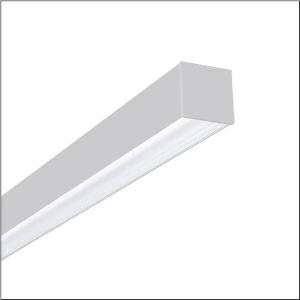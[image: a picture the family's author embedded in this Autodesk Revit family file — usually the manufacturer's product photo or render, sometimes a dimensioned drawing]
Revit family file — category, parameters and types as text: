
# Revit family: silica_r_5mx31bd1w4a_74d2
name_source: partatom
category: Lighting Fixtures
units: mm (PartAtom-declared; Revit-internal decimal feet)

## family parameters
Cut with Voids When Loaded = No
Host = Face
Light Source = No
Part Type = Normal
Room Calculation Point = No
Round Connector Dimension = Use Diameter
Shared = No

## types (1)
- --- (1 x LED, 7070 lm, 45.6 W, 4000K)
    Apparent Load = 46 VA
    CIE Flux Codes = 82 97 100 70 100
    Color Rendering = 80
    Color Temperature = 4000K
    Default Elevation = 1800 mm
    Description = Silica®, office luminaire, of aluminium, light emission: direct/indirect distribution, primary light characteristic: symmetric, installation type: suspended mounting, LED, rated luminous flux: 7.070lm, luminous efficacy: 155lm/W, light colour: 840, colour temperature: 4000K, control gear: DALI (with two DALI addresses), with terminal, 3+2-pole, max. 2.5mm², mains connection: 230V, AC, 50/60Hz, connection cable inclusive, cable length: 1,5m, rated input power: 46W, luminaire housing, of aluminium, traffic white (RAL 9016), length: 1.442mm, width: 65mm, height: 64mm, protection rating (complete): IP20, insulation class (complete): insulation class I (protective earthing), certification: CE, permissible operating ambient temperature: 0..+35°C, standard: EN 50419, packaging unit: 1 piece
    Height = 64 mm
    Lamp = 1 x LED
    Lamp Light Flux = 7070 lm
    Lamp Power = 45.6 W
    Lamp count = 1
    Length = 1442 mm
    Luminous efficacy = 155 lm/W
    Manufacturer = Siteco
    ModVariant = No
    Model = 5MX31BD1W4A
    Mounting Place = Ceiling
    Mounting Type = Pendant
    Number of Poles = 1
    OnlyDefault = Yes
    Power Factor = 1
    Product Name = Silica®
    Product group = office luminaire | ceiling pendant
    ProductGroupID = 904
    Protection Class = Protection class I
    Protection Degree = IP 20
    RLX_Detail_Level = 1
    RLX_Emergency_Light_Flux = 0 lm
    RLX_Emergency_Type = 0
    RLX_Emergency_Type_DB = No
    RlxData = <blob elided: 28937 chars, md5=6a55370d>
    Socket = socket
    Standby Power = 0 W
    System Light Flux = 7070 lm
    System Power = 46 W
    Type Comments = factory setting: direct and indirect light
    Type Image = l_1003924.jpg
    URL = http://relux.com
    VarID = @adj_198509
    Voltage = 0 V
    Weight = 0.00 kg
    Width = 66 mm

## geometry (parser evidence)
native form markers: Blend x4, Sweep x14
no freeform markers — native parametric forms only
